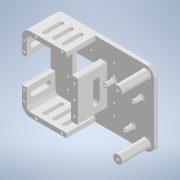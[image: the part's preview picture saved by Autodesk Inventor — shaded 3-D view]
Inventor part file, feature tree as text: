
AUTODESK INVENTOR PART (.ipt)
format: ipt  version: 2020 (Build 240168000, 168)  size: 397,312 bytes
history: native  units: mm
features: sketch x12, extrude x10, other x4, fillet x3, reference x2, hole x1, projected_geometry x1
ambient origin geometry x8: Origin, YZ Plane, XZ Plane, XY Plane, X Axis, Y Axis, Z Axis, Center Point
bodies: Solid1 (feature_tree)
feature tree (33):
  extrude  "Extrusion1"  Depth=130.0mm
  extrude  "Extrusion2"  Depth=15.0mm
  extrude  "Extrusion3"  Depth=15.0mm
  fillet  "Fillet1"  Radius=104.0mm
  extrude  "Extrusion4"  Depth=52.0mm
  extrude  "Extrusion5"  Depth=60.0mm
  sketch  "Sketch7"  dims[d17=7.5mm d18=30.0mm d19=50.0mm d20=0.0mm]
  extrude  "Extrusion6"  Depth=50.0mm
  fillet  "Fillet2"  Radius=50.0mm
  extrude  "Extrusion7"  Depth=40.0mm
  fillet  "Fillet3"  Radius=50.0mm
  hole  "Hole1"  [1 undecoded]
  extrude  "Extrusion8"  Depth=50.0mm TaperAngle=0.0deg
  extrude  "Extrusion9"  Depth=6.0mm
  extrude  "Extrusion10"  Depth=25.0mm
  sketch  "Sketch1"  dims[d0=180.0mm d1=130.0mm]
  sketch  "Sketch3"  dims[d2=7.0mm d3=0.0mm d9=15.0mm]
  sketch  "Sketch4"  dims[d10=15.0mm d11=15.0mm d12=104.0mm]
  sketch  "Sketch5"  dims[d13=52.0mm d14=75.0mm]
  projected_geometry  "Projected Loop1"
  sketch  "Sketch6"  dims[d15=12.0mm d16=60.0mm]
  sketch  "Sketch8"  dims[d21=46.0mm d22=40.0mm d23=50.0mm d24=0.0mm]
  reference  "Reference1"
  reference  "Reference2"
  sketch  "Sketch10"  dims[d25=28.0mm d26=2.0mm]
  sketch  "Sketch11"  dims[d27=8.0mm d28=50.0mm d29=0.0mm]
  sketch  "Sketch12"  dims[d30=4.0mm d31=6.0mm]
  sketch  "Sketch13"  dims[d32=25.0mm d33=25.0mm]
  sketch  "Sketch14"  dims[d34=45.0mm d35=3.5mm d36=8.0mm d37=3.5mm d38=17.0mm d39=6.0mm d40=6.0mm d41=3.5mm d42=17.0mm d43=3.5mm d44=10.0mm d45=0.0mm d46=10.0mm d47=0.0mm d48=2.0mm d49=7.0mm d50=13.0mm d51=0.0mm d52=4.0mm d53=4.0mm d54=6.0mm d55=6.3mm d56=2.0mm d57=90.0deg d58=5.0mm d59=20.594885mm d60=10.0mm d61=10.0mm d62=28.0mm d63=25.0mm d64=11.0mm d65=3.5mm d66=0.0mm d67=0.0mm d68=30.0mm d69=12.0mm d70=32.0mm d71=16.0mm d72=12.0mm d73=0.0mm d74=25.0mm d75=5.0mm d76=32.0mm d77=14.0mm d78=12.0mm d79=0.0mm]
  other  "<userpath>\Desktop\KangKangBalancing\KangKang.iam"
  other  "KangKang.iam"
  other  "Body-R:1"
  other  "bodyL:1"
note: 1 required parameter value undecoded (feature->parameter linkage not recoverable at this tier; creation-order binding heuristic only, values carry confidence <= 0.55)
